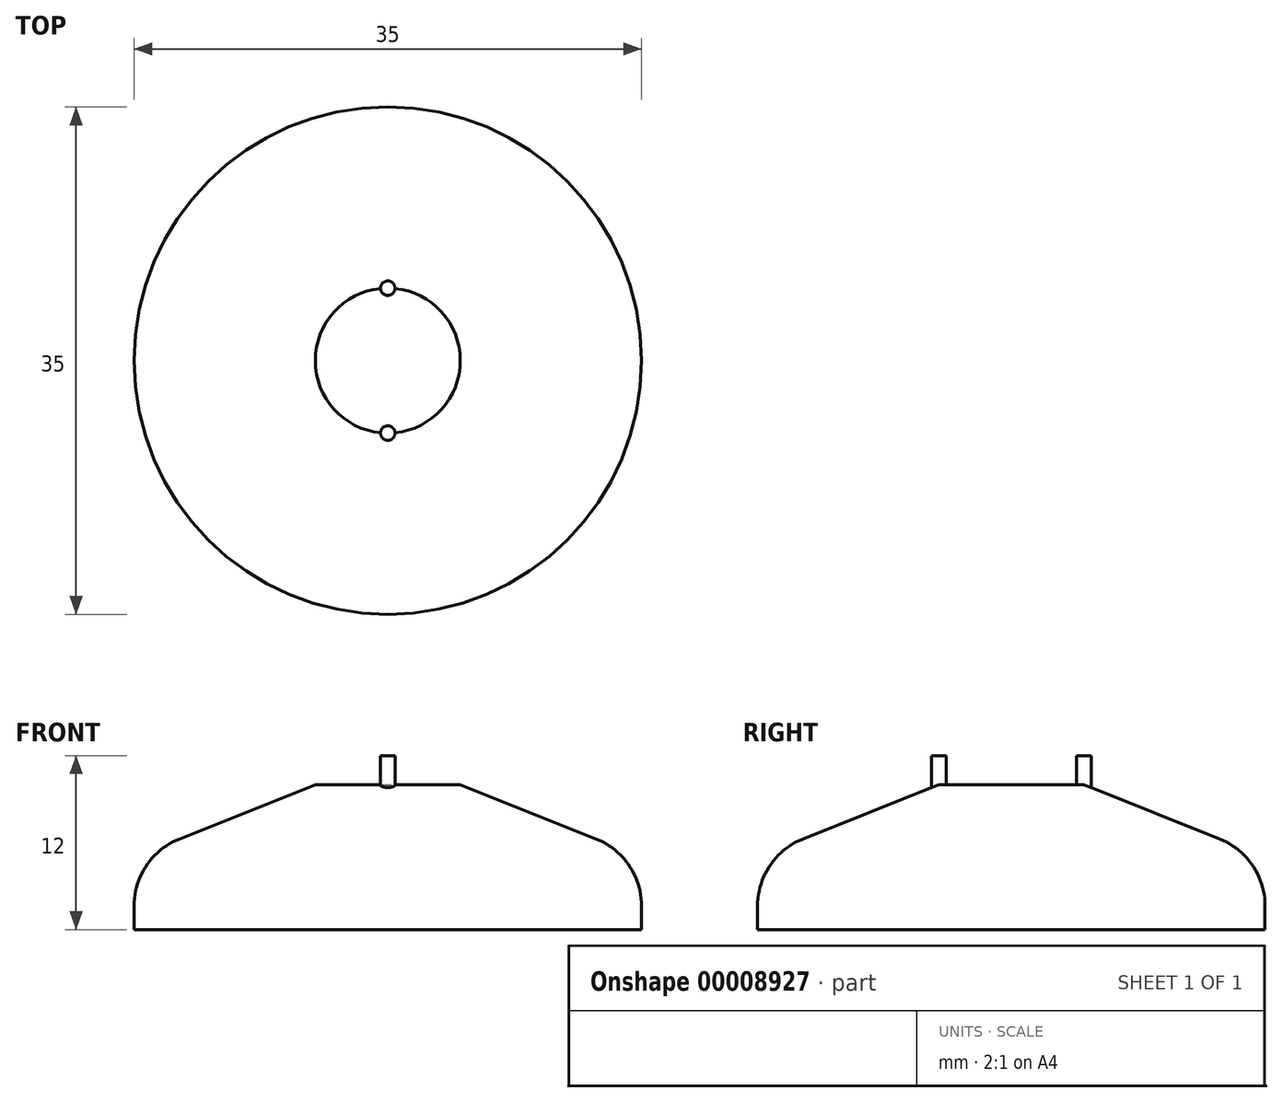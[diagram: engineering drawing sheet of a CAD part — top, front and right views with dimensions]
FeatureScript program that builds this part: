
annotation { "Feature Type Name" : "Feature", "Feature Type Description" : "" }
export const myFeature = defineFeature(function(context is Context, id is Id, definition is map)
    precondition{}
    {
        {
            var Q0;
            Q0=qCreatedBy(makeId("Front.planeOp"),FACE);
            var sketch = newSketch(context, id + "F0", { "sketchPlane" : qUnion([Q0])});
            skLineSegment(sketch, "E0", {"start": v(0, 0) * mm, "end": v(-17.5, 0) * mm});
            skLineSegment(sketch, "E1", {"start": v(-17.5, 0) * mm, "end": v(-17.5, 5) * mm});
            skLineSegment(sketch, "E2", {"start": v(-17.5, 5) * mm, "end": v(-5, 10) * mm});
            skLineSegment(sketch, "E3", {"start": v(-5, 10) * mm, "end": v(0, 10) * mm});
            skLineSegment(sketch, "E4", {"start": v(0, 10) * mm, "end": v(0, 0) * mm});
            skSolve(sketch);
        }
        {
            var Q0;
            Q0 = qSketchRegion(id + "F0", true);
            var Q1;
            Q1=sQuery(id+"F0.wireOp",EDGE,"E4");
            revolve(context, id + "F1", {"entities" : qUnion([Q0]), "axis" : qUnion([Q1]), "revolveType" : RevolveType.FULL});
        }
        {
            var Q0;
            Q0=makeQuery(id+"F1.opRevolve","SWEPT_FACE",FACE,{"disambiguationData":[OSD([sQuery(id+"F0.wireOp",EDGE,"E3")])]});
            var sketch = newSketch(context, id + "F2", { "sketchPlane" : qUnion([Q0])});
            skCircle(sketch, "E5", {"center": v(0, 5) * mm, "radius": 0.5 * mm});
            skCircle(sketch, "E6", {"center": v(0, -5) * mm, "radius": 0.5 * mm});
            skSolve(sketch);
        }
        {
            var Q0;
            Q0 = qSketchRegion(id + "F2", true);
            extrude(context, id + "F3", {"entities" : qUnion([Q0]), "operationType" : NewBodyOperationType.ADD, "depth" : 2 * mm, "hasSecondDirection" : true, "secondDirectionOppositeDirection" : true, "secondDirectionDepth" : 2 * mm});
        }
        {
            var Q0;
            Q0=makeQuery(id+"F1.opRevolve","SWEPT_EDGE",EDGE,{"disambiguationData":[OSD([sQuery(id+"F0.wireOp",EDGE,"E1"),sQuery(id+"F0.wireOp",EDGE,"E2")])]});
            fillet(context, id + "F4", {"entities" : qUnion([Q0]), "radius" : 5 * mm, "tangentPropagation" : true, "allowEdgeOverflow" : false});
        }
    });
